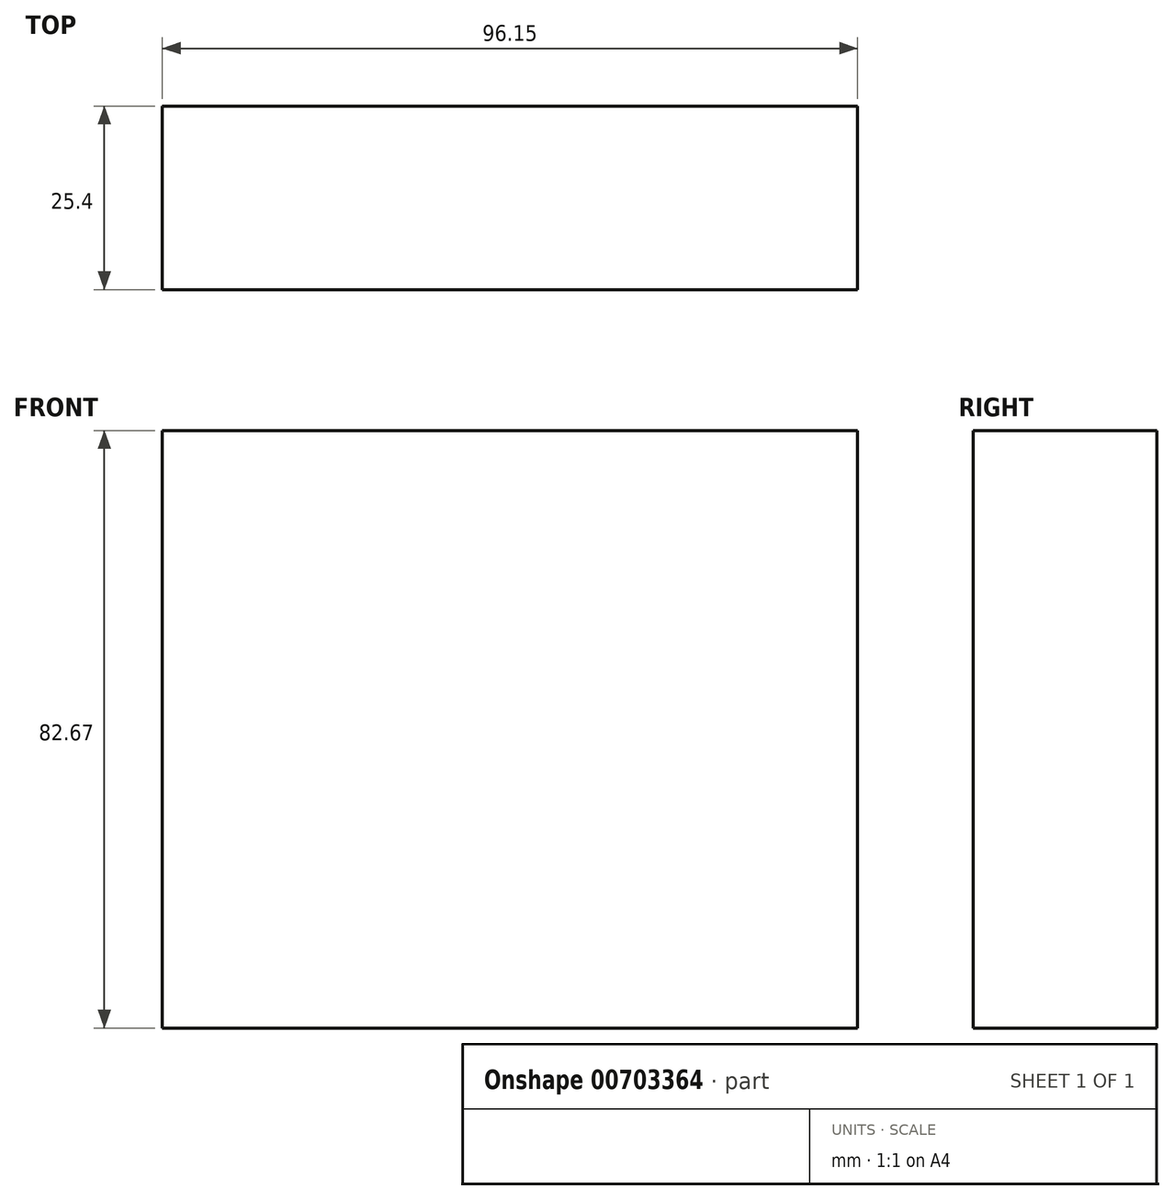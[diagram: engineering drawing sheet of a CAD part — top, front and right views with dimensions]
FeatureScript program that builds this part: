
annotation { "Feature Type Name" : "Feature", "Feature Type Description" : "" }
export const myFeature = defineFeature(function(context is Context, id is Id, definition is map)
    precondition{}
    {
        {
            var Q0;
            Q0=qCreatedBy(makeId("Front.planeOp"),FACE);
            var sketch = newSketch(context, id + "F0", { "sketchPlane" : qUnion([Q0])});
            skLineSegment(sketch, "E0.bottom", {"start": v(-41.74, 47.67) * mm, "end": v(54.41, 47.67) * mm});
            skLineSegment(sketch, "E0.top", {"start": v(-41.74, -35) * mm, "end": v(54.41, -35) * mm});
            skLineSegment(sketch, "E0.left", {"start": v(-41.74, 47.67) * mm, "end": v(-41.74, -35) * mm});
            skLineSegment(sketch, "E0.right", {"start": v(54.41, 47.67) * mm, "end": v(54.41, -35) * mm});
            skSolve(sketch);
        }
        {
            var Q0;
            Q0=makeQuery(id+"F0.imprint","IMPRINT",FACE,{"disambiguationData":[TD([[makeQuery(id+"F0.imprint","IMPRINT",EDGE,{"derivedFrom":sQuery(id+"F0.wireOp",EDGE,"E0.bottom")}),-1.0]])]});
            extrude(context, id + "F1", {"entities" : qUnion([Q0]), "depth" : 25.4 * mm, "offsetDistance" : 25.4 * mm});
        }
    });
